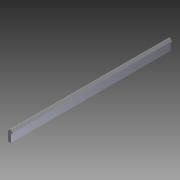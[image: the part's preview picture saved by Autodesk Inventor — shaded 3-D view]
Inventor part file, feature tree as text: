
AUTODESK INVENTOR PART (.ipt)
format: ipt  version: 2014 (Build 180170000, 170)  size: 95,232 bytes
history: native  units: in
note: dims shown in document units (in); Inventor stores cm internally (conversion verified against a paired STEP export)
features: fillet x1, other x1, imported_body x1
ambient origin geometry x8: Origin, YZ Plane, XZ Plane, XY Plane, X Axis, Y Axis, Z Axis, Center Point
bodies: Body1 (feature_tree)
feature tree (3):
  fillet  "Fillet1"  [1 undecoded]
  other  "BWC-T3-SS-11"
  imported_body  "Base1"
note: 1 required parameter value undecoded (feature->parameter linkage not recoverable at this tier; creation-order binding heuristic only, values carry confidence <= 0.55)
